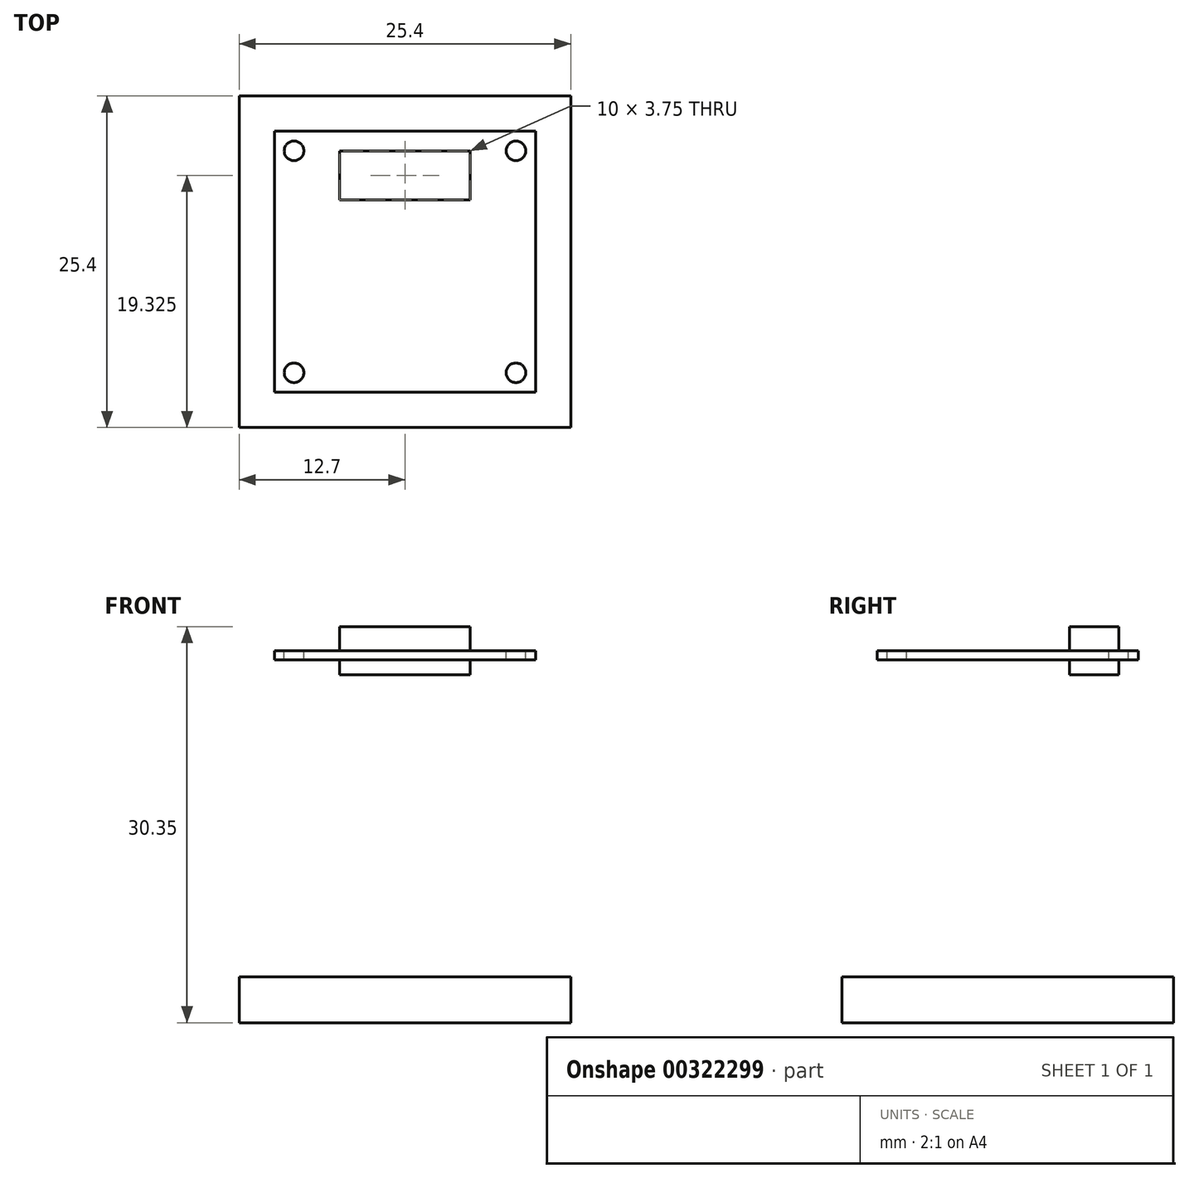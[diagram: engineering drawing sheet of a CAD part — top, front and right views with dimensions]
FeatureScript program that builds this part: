
annotation { "Feature Type Name" : "Feature", "Feature Type Description" : "" }
export const myFeature = defineFeature(function(context is Context, id is Id, definition is map)
    precondition{}
    {
        {
            var Q0;
            Q0=qCreatedBy(makeId("Top.planeOp"),FACE);
            var sketch = newSketch(context, id + "F0", { "sketchPlane" : qUnion([Q0])});
            skLineSegment(sketch, "E0.bottom", {"start": v(-10, 10) * mm, "end": v(10, 10) * mm});
            skLineSegment(sketch, "E0.top", {"start": v(-10, -10) * mm, "end": v(10, -10) * mm});
            skLineSegment(sketch, "E0.left", {"start": v(-10, 10) * mm, "end": v(-10, -10) * mm});
            skLineSegment(sketch, "E0.right", {"start": v(10, 10) * mm, "end": v(10, -10) * mm});
            skPoint(sketch, "E0.middle", {"position": v(0, 0) * mm});
            skLineSegment(sketch, "E1.bottom", {"start": v(-8.5, 8.5) * mm, "end": v(8.5, 8.5) * mm, "construction": true});
            skLineSegment(sketch, "E1.top", {"start": v(-8.5, -8.5) * mm, "end": v(8.5, -8.5) * mm, "construction": true});
            skLineSegment(sketch, "E1.left", {"start": v(-8.5, 8.5) * mm, "end": v(-8.5, -8.5) * mm, "construction": true});
            skLineSegment(sketch, "E1.right", {"start": v(8.5, 8.5) * mm, "end": v(8.5, -8.5) * mm, "construction": true});
            skLineSegment(sketch, "E2.bottom", {"start": v(-5, 8.5) * mm, "end": v(5, 8.5) * mm});
            skLineSegment(sketch, "E2.top", {"start": v(-5, 4.75) * mm, "end": v(5, 4.75) * mm});
            skLineSegment(sketch, "E2.left", {"start": v(-5, 8.5) * mm, "end": v(-5, 4.75) * mm});
            skLineSegment(sketch, "E2.right", {"start": v(5, 8.5) * mm, "end": v(5, 4.75) * mm});
            skPoint(sketch, "E3", {"position": v(0, 4.75) * mm});
            skSolve(sketch);
        }
        {
            var Q0;
            Q0=qSketchRegion(id+"F0",true);
            var Q1;
            Q1=makeQuery(id+"F0.imprint","IMPRINT",FACE,{"disambiguationData":[TD([[makeQuery(id+"F0.imprint","IMPRINT",EDGE,{"derivedFrom":sQuery(id+"F0.wireOp",EDGE,"E2.bottom")}),-1.0]])]});
            extrude(context, id + "F1", {"entities" : qUnion([Q0, Q1]), "oppositeDirection" : true, "depth" : .7 * mm});
        }
        {
            var Q0;
            Q0=sQuery(id+"F0.wireOp",VERTEX,"E1.left.start");
            var Q1;
            Q1=sQuery(id+"F0.wireOp",VERTEX,"E1.bottom.end");
            var Q2;
            Q2=sQuery(id+"F0.wireOp",VERTEX,"E1.right.end");
            var Q3;
            Q3=sQuery(id+"F0.wireOp",VERTEX,"E1.left.end");
            var Q4;
            Q4=makeQuery(id+"F1.opExtrude","SWEPT_BODY",BODY,{"disambiguationData":[OSD([sQuery(id+"F0.wireOp",EDGE,"E0.bottom"),sQuery(id+"F0.wireOp",EDGE,"E0.top"),sQuery(id+"F0.wireOp",EDGE,"E0.left"),sQuery(id+"F0.wireOp",EDGE,"E0.right")])]});
            hole(context, id + "F2", {"style" : HoleStyle.SIMPLE, "endStyle" : HoleEndStyle.THROUGH, "holeDiameter" : 1.5 * mm, "tappedDepth" : 12.7 * mm, "tapClearance" : 3, "locations" : qUnion([Q0, Q1, Q2, Q3]), "scope" : qUnion([Q4])});
        }
        {
            var Q0;
            Q0=qCreatedBy(makeId("Top.planeOp"),FACE);
            var sketch = newSketch(context, id + "F3", { "sketchPlane" : qUnion([Q0])});
            skLineSegment(sketch, "E4.0", {"start": v(-5, 8.5) * mm, "end": v(5, 8.5) * mm});
            skLineSegment(sketch, "E4.1", {"start": v(5, 8.5) * mm, "end": v(5, 4.75) * mm});
            skLineSegment(sketch, "E4.2", {"start": v(-5, 4.75) * mm, "end": v(5, 4.75) * mm});
            skLineSegment(sketch, "E4.3", {"start": v(-5, 8.5) * mm, "end": v(-5, 4.75) * mm});
            skSolve(sketch);
        }
        {
            var Q0;
            Q0=qSketchRegion(id+"F3",true);
            extrude(context, id + "F4", {"entities" : qUnion([Q0]), "operationType" : NewBodyOperationType.ADD, "endBound" : BoundingType.SYMMETRIC, "depth" : 3.7 * mm});
        }
        {
            var Q0;
            Q0=qCreatedBy(makeId("Top.planeOp"),FACE);
            cPlane(context, id + "F5", {"entities" : qUnion([Q0]), "cplaneType" : CPlaneType.OFFSET, "offset" : 25 * mm, "oppositeDirection" : true, "width" : 150 * mm, "height" : 150 * mm});
        }
        {
            var Q0;
            Q0=qCreatedBy(id+"F5.planeOp",FACE);
            var sketch = newSketch(context, id + "F6", { "sketchPlane" : qUnion([Q0])});
            skLineSegment(sketch, "E5.bottom", {"start": v(-12.7, -12.7) * mm, "end": v(12.7, -12.7) * mm});
            skLineSegment(sketch, "E5.top", {"start": v(-12.7, 12.7) * mm, "end": v(12.7, 12.7) * mm});
            skLineSegment(sketch, "E5.left", {"start": v(-12.7, -12.7) * mm, "end": v(-12.7, 12.7) * mm});
            skLineSegment(sketch, "E5.right", {"start": v(12.7, -12.7) * mm, "end": v(12.7, 12.7) * mm});
            skPoint(sketch, "E5.middle", {"position": v(0, 0) * mm});
            skSolve(sketch);
        }
        {
            var Q0;
            Q0=makeQuery(id+"F6.imprint","IMPRINT",FACE,{"disambiguationData":[TD([[makeQuery(id+"F6.imprint","IMPRINT",EDGE,{"derivedFrom":sQuery(id+"F6.wireOp",EDGE,"E5.bottom")}),1.0]])]});
            extrude(context, id + "F7", {"entities" : qUnion([Q0]), "oppositeDirection" : true, "depth" : 3.5 * mm});
        }
    });
